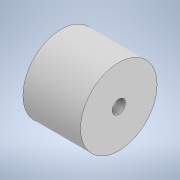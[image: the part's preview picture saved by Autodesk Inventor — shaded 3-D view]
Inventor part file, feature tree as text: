
AUTODESK INVENTOR PART (.ipt)
format: ipt  version: 2021 (Build 250183000, 183)  size: 155,648 bytes
history: native  units: mm
features: other x3, extrude x2, sketch x2, projected_geometry x2
ambient origin geometry x8: Origin, YZ Plane, XZ Plane, XY Plane, X Axis, Y Axis, Z Axis, Center Point
bodies: Solid1 (feature_tree)
feature tree (9):
  other  "wheel_adapter_inner.ipt"
  extrude  "Extrusion1"  Depth=10.0mm TaperAngle=0.0deg
  extrude  "Extrusion2"  [1 undecoded]
  other  "Solid1::wheel_adapter_inner.ipt"
  other  "TaggingFeature1"
  sketch  "Sketch1"  dims[d0=10.0mm d1=10.0mm d2=0.0mm]
  projected_geometry  "Projected Loop1"
  sketch  "Sketch2"  dims[d3=10.0mm d4=0.0mm]
  projected_geometry  "Projected Loop2"
note: 1 required parameter value undecoded (feature->parameter linkage not recoverable at this tier; creation-order binding heuristic only, values carry confidence <= 0.55)
